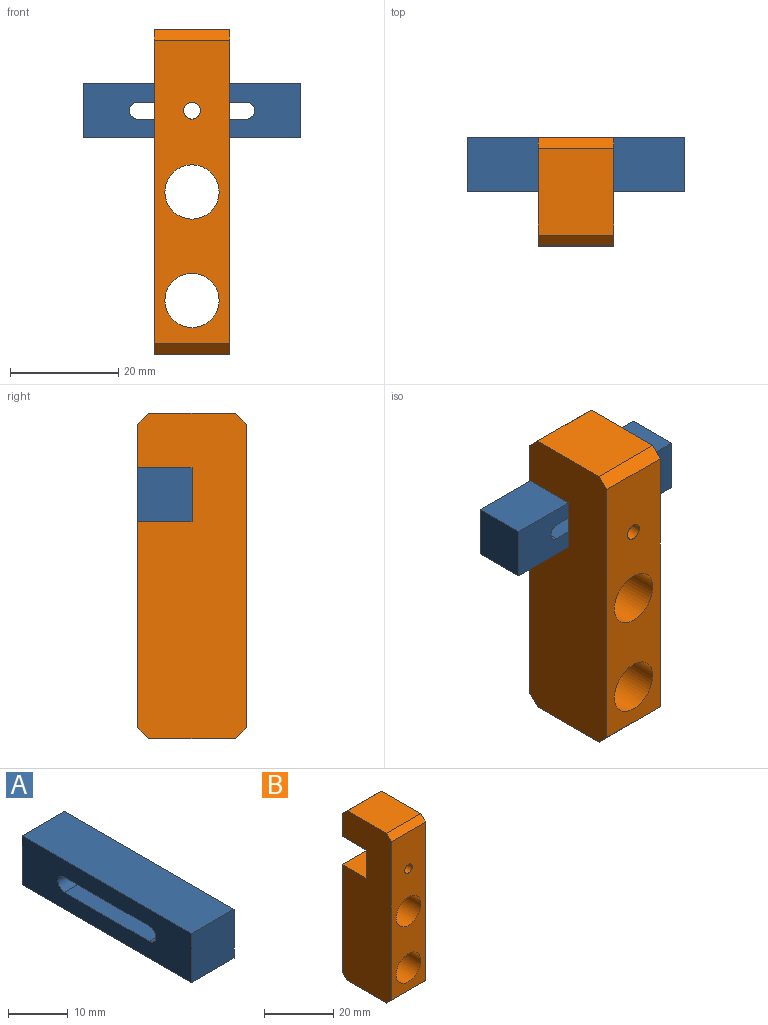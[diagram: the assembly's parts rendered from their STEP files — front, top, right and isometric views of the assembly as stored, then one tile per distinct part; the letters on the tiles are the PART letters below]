
ASSEMBLY  parts=2 mates=2
PART A: 10 faces, bbox 10x40x10 mm
  f0: plane 40x10mm, normal (1,0,0), area 330.5mm2, adj f1,f3,f4,f5,f6,f7,f8,f9
  f1: plane 40x10mm, normal (0,0,1), area 400mm2, adj f0,f2,f4,f5
  f2: plane 40x10mm, normal (-1,0,0), area 330.5mm2, adj f1,f3,f4,f5,f6,f7,f8,f9
  f3: plane 40x10mm, normal (0,0,-1), area 400mm2, adj f0,f2,f4,f5
  f4: plane 10x10mm, normal (0,-1,0), area 100mm2, adj f0,f1,f2,f3
  f5: plane 10x10mm, normal (0,1,0), area 100mm2, adj f0,f1,f2,f3
  f6: plane 20x10mm, normal (0,0,1), area 200mm2, adj f0,f2,f7,f8
  f7: cylinder r=1.55mm len=10mm, axis (1,0,0), area 48.7mm2, adj f0,f2,f6,f9
  f8: cylinder r=1.55mm len=10mm, axis (1,0,0), area 48.7mm2, adj f0,f2,f6,f9
  f9: plane 20x10mm, normal (0,0,-1), area 200mm2, adj f0,f2,f7,f8
PART B: 17 faces, bbox 14x20x60 mm
  f0: plane 14x8mm, normal (0,1,0), area 112mm2, adj f1,f2,f9,f15
  f1: plane 60x20mm, normal (1,0,0), area 1092mm2, adj f0,f3,f5,f7,f8,f9,f10,f11
  f2: plane 60x20mm, normal (-1,0,0), area 1092mm2, adj f0,f3,f5,f7,f8,f9,f10,f11
  f3: plane 16x14mm, normal (0,0,-1), area 224mm2, adj f1,f2,f12,f13
  f4: cylinder r=5mm len=20mm, axis (0,1,0), area 628.3mm2, adj f7,f8
  f5: plane 16x14mm, normal (0,0,1), area 224mm2, adj f1,f2,f14,f15
  f6: cylinder r=5mm len=20mm, axis (0,1,0), area 628.3mm2, adj f7,f8
  f7: plane 56x14mm, normal (0,-1,0), area 619.4mm2, adj f1,f2,f4,f6,f13,f14,f16
  f8: plane 38x14mm, normal (0,1,0), area 374.9mm2, adj f1,f2,f4,f6,f11,f12
  f9: plane 14x10mm, normal (0,0,-1), area 140mm2, adj f0,f1,f2,f10
  f10: plane 14x10mm, normal (0,1,0), area 132.5mm2, adj f1,f2,f9,f11,f16
  f11: plane 14x10mm, normal (0,0,1), area 140mm2, adj f1,f2,f8,f10
  f12: plane 14x2mm, normal (0,0.71,-0.71), area 39.6mm2, adj f1,f2,f3,f8
  f13: plane 14x2mm, normal (0,-0.71,-0.71), area 39.6mm2, adj f1,f2,f3,f7
  f14: plane 14x2mm, normal (0,-0.71,0.71), area 39.6mm2, adj f1,f2,f5,f7
  f15: plane 14x2mm, normal (0,0.71,0.71), area 39.6mm2, adj f0,f1,f2,f5
  f16: cylinder r=1.55mm len=10mm, axis (0,1,0), area 97.4mm2, adj f7,f10
PLACE A rot(axis=(0,0,1),90deg) t=(-32.31,13.36,54.7)mm
PLACE B t=(-12.31,18.36,9.7)mm
MATE parallel B.f9 <-> A.f1  axis (0,0,-1) through (-12.31,13.36,59.7)mm
MATE parallel A.f2 <-> B.f10  axis (0,-1,0) through (-32.31,8.36,54.7)mm
